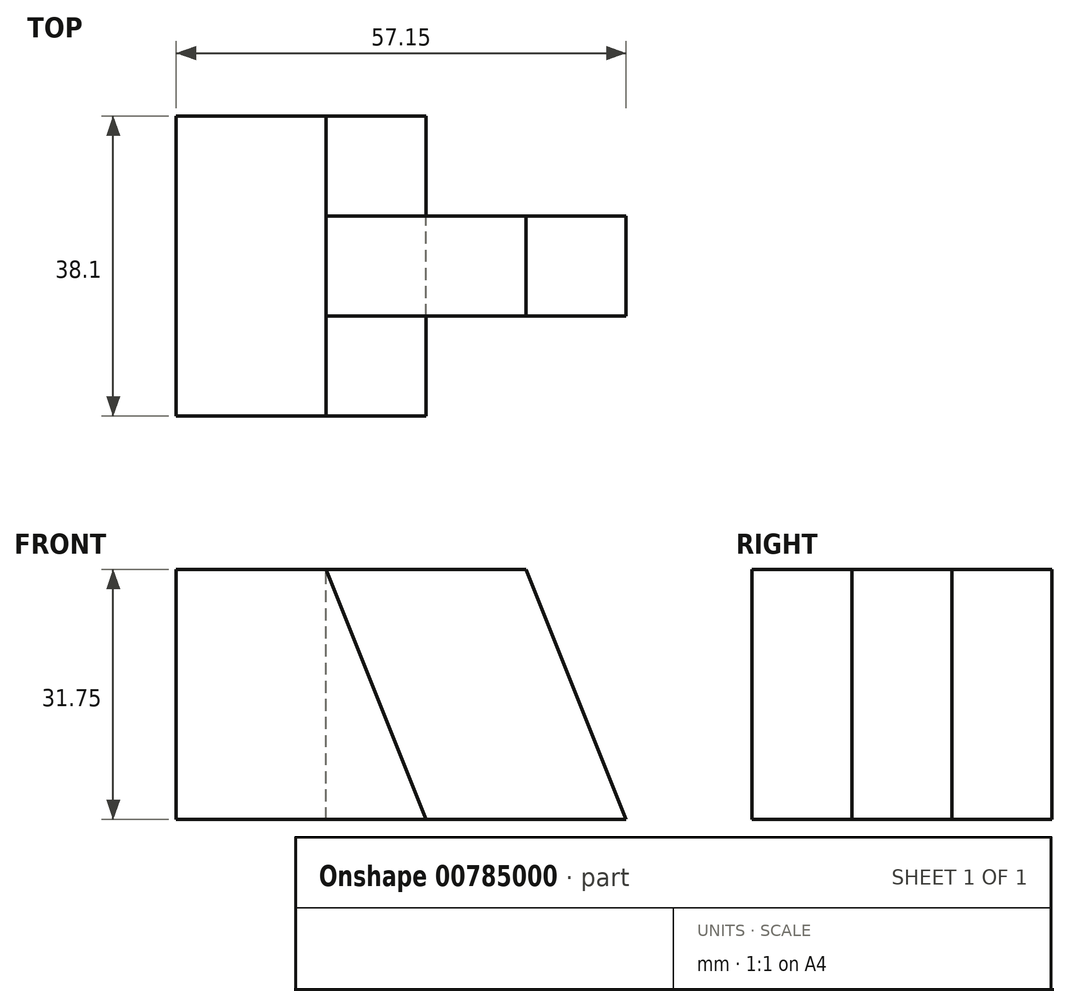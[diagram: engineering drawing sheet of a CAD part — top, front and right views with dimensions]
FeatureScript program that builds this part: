
annotation { "Feature Type Name" : "Feature", "Feature Type Description" : "" }
export const myFeature = defineFeature(function(context is Context, id is Id, definition is map)
    precondition{}
    {
        {
            var Q0;
            Q0=qCreatedBy(makeId("Front.planeOp"),FACE);
            var sketch = newSketch(context, id + "F0", { "sketchPlane" : qUnion([Q0])});
            skLineSegment(sketch, "E0", {"start": v(0, 0) * mm, "end": v(57.15, 0) * mm});
            skLineSegment(sketch, "E1", {"start": v(57.15, 0) * mm, "end": v(57.15, 31.75) * mm});
            skLineSegment(sketch, "E2", {"start": v(57.15, 31.75) * mm, "end": v(0, 31.75) * mm});
            skLineSegment(sketch, "E3", {"start": v(0, 31.75) * mm, "end": v(0, 0) * mm});
            skSolve(sketch);
        }
        {
            var Q0;
            Q0 = qSketchRegion(id + "F0", true);
            extrude(context, id + "F1", {"entities" : qUnion([Q0]), "depth" : 38.1 * mm, "offsetDistance" : 25.4 * mm});
        }
        {
            var Q0;
            Q0=makeQuery(id+"F1.opExtrude","SWEPT_FACE",FACE,{"disambiguationData":[OSD([sQuery(id+"F0.wireOp",EDGE,"E2")])]});
            var sketch = newSketch(context, id + "F2", { "sketchPlane" : qUnion([Q0])});
            skLineSegment(sketch, "E4", {"start": v(0, 0) * mm, "end": v(19.05, 0) * mm});
            skLineSegment(sketch, "E5", {"start": v(19.05, 0) * mm, "end": v(19.05, -12.7) * mm});
            skLineSegment(sketch, "E6", {"start": v(19.05, -12.7) * mm, "end": v(57.15, -12.7) * mm});
            skLineSegment(sketch, "E7", {"start": v(0, -38.1) * mm, "end": v(19.05, -38.1) * mm});
            skLineSegment(sketch, "E8", {"start": v(19.05, -38.1) * mm, "end": v(19.05, -25.4) * mm});
            skLineSegment(sketch, "E9", {"start": v(19.05, -25.4) * mm, "end": v(57.15, -25.4) * mm});
            skSolve(sketch);
        }
        {
            var Q0;
            Q0 = qSketchRegion(id + "F2", true);
            var Q1;
            {var subQ0=sQuery(id+"F2.wireOp",EDGE,"E8");Q1=makeQuery(id+"F2.imprint","IMPRINT",FACE,{"disambiguationData":[TD([[makeQuery(id+"F2.imprint","IMPRINT",EDGE,{"derivedFrom":subQ0}),-1.0]])]});}
            var Q2;
            {var subQ0=sQuery(id+"F2.wireOp",EDGE,"E5");Q2=makeQuery(id+"F2.imprint","IMPRINT",FACE,{"disambiguationData":[TD([[makeQuery(id+"F2.imprint","IMPRINT",EDGE,{"derivedFrom":subQ0}),1.0]])]});}
            extrude(context, id + "F3", {"entities" : qUnion([Q0, Q1, Q2]), "operationType" : NewBodyOperationType.REMOVE, "oppositeDirection" : true, "depth" : 31.75 * mm, "offsetDistance" : 25.4 * mm});
        }
        {
            var Q0;
            Q0=makeQuery(id+"F3.boolean.opBoolean","COPY",FACE,{"derivedFrom":makeQuery(id+"F3.opExtrude","SWEPT_FACE",FACE,{"disambiguationData":[OSD([sQuery(id+"F2.wireOp",EDGE,"E9")])]})});
            var sketch = newSketch(context, id + "F4", { "sketchPlane" : qUnion([Q0])});
            skLineSegment(sketch, "E10", {"start": v(19.05, 0) * mm, "end": v(31.75, 0) * mm});
            skLineSegment(sketch, "E11", {"start": v(31.75, 0) * mm, "end": v(19.05, 31.75) * mm});
            skSolve(sketch);
        }
        {
            var Q0;
            Q0 = qSketchRegion(id + "F4", true);
            var Q1;
            Q1=makeQuery(id+"F4.imprint","IMPRINT",FACE,{"disambiguationData":[TD([[makeQuery(id+"F4.imprint","IMPRINT",EDGE,{"derivedFrom":sQuery(id+"F4.wireOp",EDGE,"E10")}),1.0]])]});
            extrude(context, id + "F5", {"entities" : qUnion([Q0, Q1]), "operationType" : NewBodyOperationType.ADD, "depth" : 12.7 * mm, "offsetDistance" : 25.4 * mm});
        }
        {
            var Q0;
            Q0=makeQuery(id+"F1.opExtrude","CAP_FACE",FACE,{"disambiguationData":[OSD([sQuery(id+"F0.wireOp",EDGE,"E0"),sQuery(id+"F0.wireOp",EDGE,"E1"),sQuery(id+"F0.wireOp",EDGE,"E2"),sQuery(id+"F0.wireOp",EDGE,"E3")])],"isStart":true});
            var sketch = newSketch(context, id + "F6", { "sketchPlane" : qUnion([Q0])});
            skLineSegment(sketch, "E12", {"start": v(-19.05, 0) * mm, "end": v(-31.75, 0) * mm});
            skLineSegment(sketch, "E13", {"start": v(-31.75, 0) * mm, "end": v(-19.05, 31.75) * mm});
            skSolve(sketch);
        }
        {
            var Q0;
            Q0=makeQuery(id+"F6.imprint","IMPRINT",FACE,{"disambiguationData":[TD([[makeQuery(id+"F6.imprint","IMPRINT",EDGE,{"derivedFrom":sQuery(id+"F6.wireOp",EDGE,"E12")}),-1.0]])]});
            extrude(context, id + "F7", {"entities" : qUnion([Q0]), "oppositeDirection" : true, "depth" : 25.4 * mm, "offsetDistance" : 25.4 * mm});
        }
        {
            var Q0;
            Q0=makeQuery(id+"F3.boolean.opBoolean","COPY",FACE,{"derivedFrom":makeQuery(id+"F3.opExtrude","SWEPT_FACE",FACE,{"disambiguationData":[OSD([sQuery(id+"F2.wireOp",EDGE,"E9")])]})});
            var sketch = newSketch(context, id + "F8", { "sketchPlane" : qUnion([Q0])});
            skLineSegment(sketch, "E14", {"start": v(44.45, 31.75) * mm, "end": v(57.15, 0) * mm});
            skLineSegment(sketch, "E15", {"start": v(44.45, 31.75) * mm, "end": v(57.15, 31.75) * mm});
            skLineSegment(sketch, "E16", {"start": v(57.15, 31.75) * mm, "end": v(57.15, 0) * mm});
            skSolve(sketch);
        }
        {
            var Q0;
            Q0 = qSketchRegion(id + "F8", true);
            extrude(context, id + "F9", {"entities" : qUnion([Q0]), "operationType" : NewBodyOperationType.REMOVE, "oppositeDirection" : true, "depth" : 25.4 * mm, "offsetDistance" : 25.4 * mm});
        }
    });
